# Revit family: Toilet-Floor_Mount-KOHLER-Memoirs_Stately-K-33817_1
name_source: partatom
category: Plumbing Fixtures
units: mm (PartAtom-declared; Revit-internal decimal feet)

## family parameters
Cut with Voids When Loaded = No
Host = Face
OmniClass Number = 23.31.19.00
OmniClass Title = Toilets
Part Type = Normal
Room Calculation Point = No
Round Connector Dimension = Use Diameter
Shared = No

## types (2) — shared parameters
ADA Compliant = No
Assembly Code = D2010100
Bowl Height = 16 1/2"
CW Connection = Yes
Cold Water Inlet = Cold Water Inlet
Date Modified = 07/29/2022
Default Elevation = 0"
Description = CONCEALED CC CH 128 Toilet Elongated Bowl
Flow Rate = 0 GPM
Flush Rate- GPF = GPF
Flush Rate- LPF = LPF
HW Connection = No
Height = 31 1/8"
Hot Water Inlet = Hot Water Inlet
Length = 29 7/16"
Manufacturer = Kohler Co.
Master Format 2014 = 22 42 13.13
Master Format 2014 Name = Residential Water Closets
Material = Vitreous China
Pressure = 0.00 psi
Product Documentation Link = https://www.us.kohler.com
Product Name = Memoirs_Stately
Product Page URL = http://www.us.kohler.com
Rough-In = 12"
Seat Included = Yes
URL = https://www.us.kohler.com
Vent Connection = No
Waste Connection = Yes
Waste Water Outlet = Waste Water Outlet
WaterSense Certified = No
Width = 18 7/8"

## per-type parameters (varying)
| type | Finish | Model | Type |
| 0-White | Kohler-Vitreous_China-0-White | K-33817-0 | 1 |
| 96-Biscuit | Kohler-Vitreous_China-96-Biscuit | K-33817-96 | 2 |

## geometry (parser evidence)
native form markers: Sweep x5
no freeform markers — native parametric forms only
